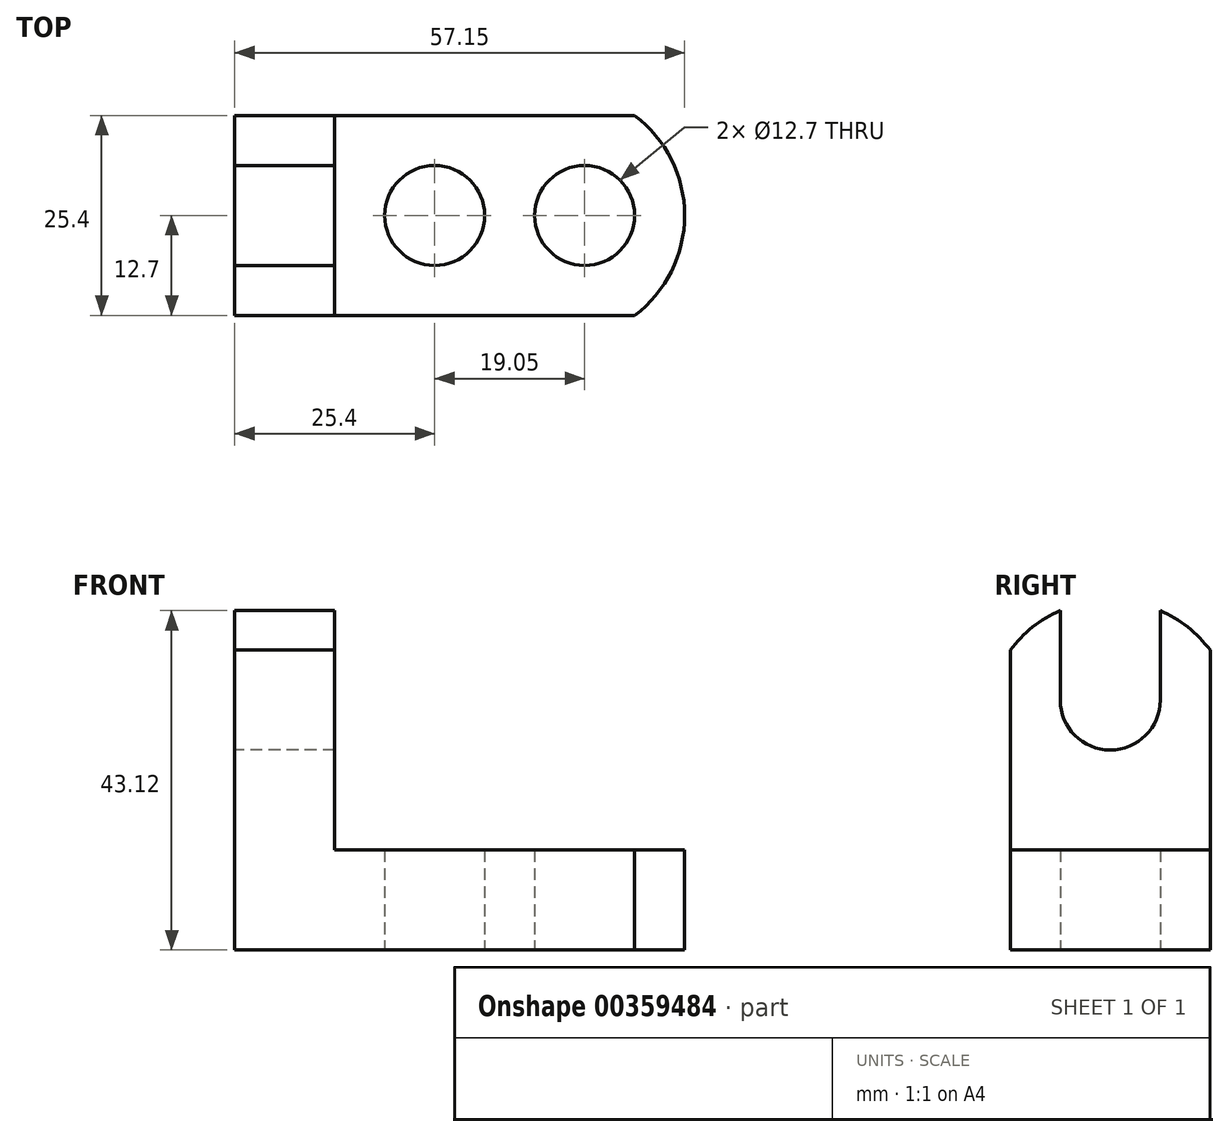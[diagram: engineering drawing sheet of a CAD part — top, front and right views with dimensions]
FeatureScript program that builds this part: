
annotation { "Feature Type Name" : "Feature", "Feature Type Description" : "" }
export const myFeature = defineFeature(function(context is Context, id is Id, definition is map)
    precondition{}
    {
        {
            var Q0;
            Q0=qCreatedBy(makeId("Front.planeOp"),FACE);
            var sketch = newSketch(context, id + "F0", { "sketchPlane" : qUnion([Q0])});
            skLineSegment(sketch, "E0", {"start": v(0, 44.45) * mm, "end": v(0, 0) * mm});
            skLineSegment(sketch, "E1", {"start": v(0, 0) * mm, "end": v(57.15, 0) * mm});
            skLineSegment(sketch, "E2", {"start": v(57.15, 0) * mm, "end": v(57.15, 44.45) * mm});
            skLineSegment(sketch, "E3", {"start": v(57.15, 44.45) * mm, "end": v(0, 44.45) * mm});
            skSolve(sketch);
        }
        {
            var Q0;
            Q0 = qSketchRegion(id + "F0", true);
            extrude(context, id + "F1", {"entities" : qUnion([Q0]), "oppositeDirection" : true, "depth" : 25.4 * mm});
        }
        {
            var Q0;
            Q0=qCreatedBy(makeId("Front.planeOp"),FACE);
            var sketch = newSketch(context, id + "F2", { "sketchPlane" : qUnion([Q0])});
            skLineSegment(sketch, "E4", {"start": v(12.7, 44.45) * mm, "end": v(12.7, 12.7) * mm});
            skLineSegment(sketch, "E5", {"start": v(12.7, 12.7) * mm, "end": v(57.15, 12.7) * mm});
            skLineSegment(sketch, "E6", {"start": v(57.15, 12.7) * mm, "end": v(57.15, 44.45) * mm});
            skLineSegment(sketch, "E7", {"start": v(57.15, 44.45) * mm, "end": v(12.7, 44.45) * mm});
            skSolve(sketch);
        }
        {
            var Q0;
            Q0 = qSketchRegion(id + "F2", true);
            extrude(context, id + "F3", {"entities" : qUnion([Q0]), "operationType" : NewBodyOperationType.REMOVE, "oppositeDirection" : true, "depth" : 25.4 * mm});
        }
        {
            var Q0;
            Q0=qCreatedBy(makeId("Top.planeOp"),FACE);
            var sketch = newSketch(context, id + "F4", { "sketchPlane" : qUnion([Q0])});
            skArc(sketch, "E8", {"start": v(50.8, 0) * mm, "mid": v(57.15, 12.7) * mm, "end": v(50.8, 25.4) * mm});
            skLineSegment(sketch, "E9", {"start": v(50.8, 25.4) * mm, "end": v(57.15, 25.4) * mm});
            skLineSegment(sketch, "E10", {"start": v(57.15, 25.4) * mm, "end": v(57.15, 0) * mm});
            skLineSegment(sketch, "E11", {"start": v(57.15, 0) * mm, "end": v(50.8, 0) * mm});
            skLineSegment(sketch, "E12", {"start": v(50.8, 0) * mm, "end": v(57.15, 0) * mm});
            skSolve(sketch);
        }
        {
            var Q0;
            Q0 = qSketchRegion(id + "F4", true);
            extrude(context, id + "F5", {"entities" : qUnion([Q0]), "operationType" : NewBodyOperationType.REMOVE, "depth" : 25.4 * mm});
        }
        {
            var Q0;
            Q0=qCreatedBy(makeId("Top.planeOp"),FACE);
            var sketch = newSketch(context, id + "F6", { "sketchPlane" : qUnion([Q0])});
            skCircle(sketch, "E13", {"center": v(25.4, 12.7) * mm, "radius": 6.35 * mm});
            skCircle(sketch, "E14", {"center": v(44.45, 12.7) * mm, "radius": 6.35 * mm});
            skSolve(sketch);
        }
        {
            var Q0;
            Q0 = qSketchRegion(id + "F6", true);
            extrude(context, id + "F7", {"entities" : qUnion([Q0]), "operationType" : NewBodyOperationType.REMOVE, "depth" : 25.4 * mm});
        }
        {
            var Q0;
            Q0=qCreatedBy(makeId("Right.planeOp"),FACE);
            var sketch = newSketch(context, id + "F8", { "sketchPlane" : qUnion([Q0])});
            skLineSegment(sketch, "E15", {"start": v(6.35, 44.45) * mm, "end": v(6.35, 31.75) * mm});
            skLineSegment(sketch, "E16", {"start": v(6.35, 31.75) * mm, "end": v(6.35, 44.45) * mm});
            skLineSegment(sketch, "E17", {"start": v(19.05, 44.45) * mm, "end": v(19.05, 31.75) * mm});
            skArc(sketch, "E18", {"start": v(6.35, 31.75) * mm, "mid": v(12.7, 25.4) * mm, "end": v(19.05, 31.75) * mm});
            skLineSegment(sketch, "E19", {"start": v(6.35, 44.45) * mm, "end": v(19.05, 44.45) * mm});
            skSolve(sketch);
        }
        {
            var Q0;
            Q0 = qSketchRegion(id + "F8", true);
            extrude(context, id + "F9", {"entities" : qUnion([Q0]), "operationType" : NewBodyOperationType.REMOVE, "depth" : 25.4 * mm});
        }
        {
            var Q0;
            Q0=qCreatedBy(makeId("Right.planeOp"),FACE);
            var sketch = newSketch(context, id + "F10", { "sketchPlane" : qUnion([Q0])});
            skArc(sketch, "E20", {"start": v(25.4, 38.1) * mm, "mid": v(12.7, 44.45) * mm, "end": v(0, 38.1) * mm});
            skLineSegment(sketch, "E21", {"start": v(0, 38.1) * mm, "end": v(0, 44.45) * mm});
            skLineSegment(sketch, "E22", {"start": v(0, 44.45) * mm, "end": v(25.4, 44.45) * mm});
            skLineSegment(sketch, "E23", {"start": v(25.4, 44.45) * mm, "end": v(25.4, 38.1) * mm});
            skSolve(sketch);
        }
        {
            var Q0;
            Q0 = qSketchRegion(id + "F10", true);
            extrude(context, id + "F11", {"entities" : qUnion([Q0]), "operationType" : NewBodyOperationType.REMOVE, "depth" : 25.4 * mm});
        }
    });
